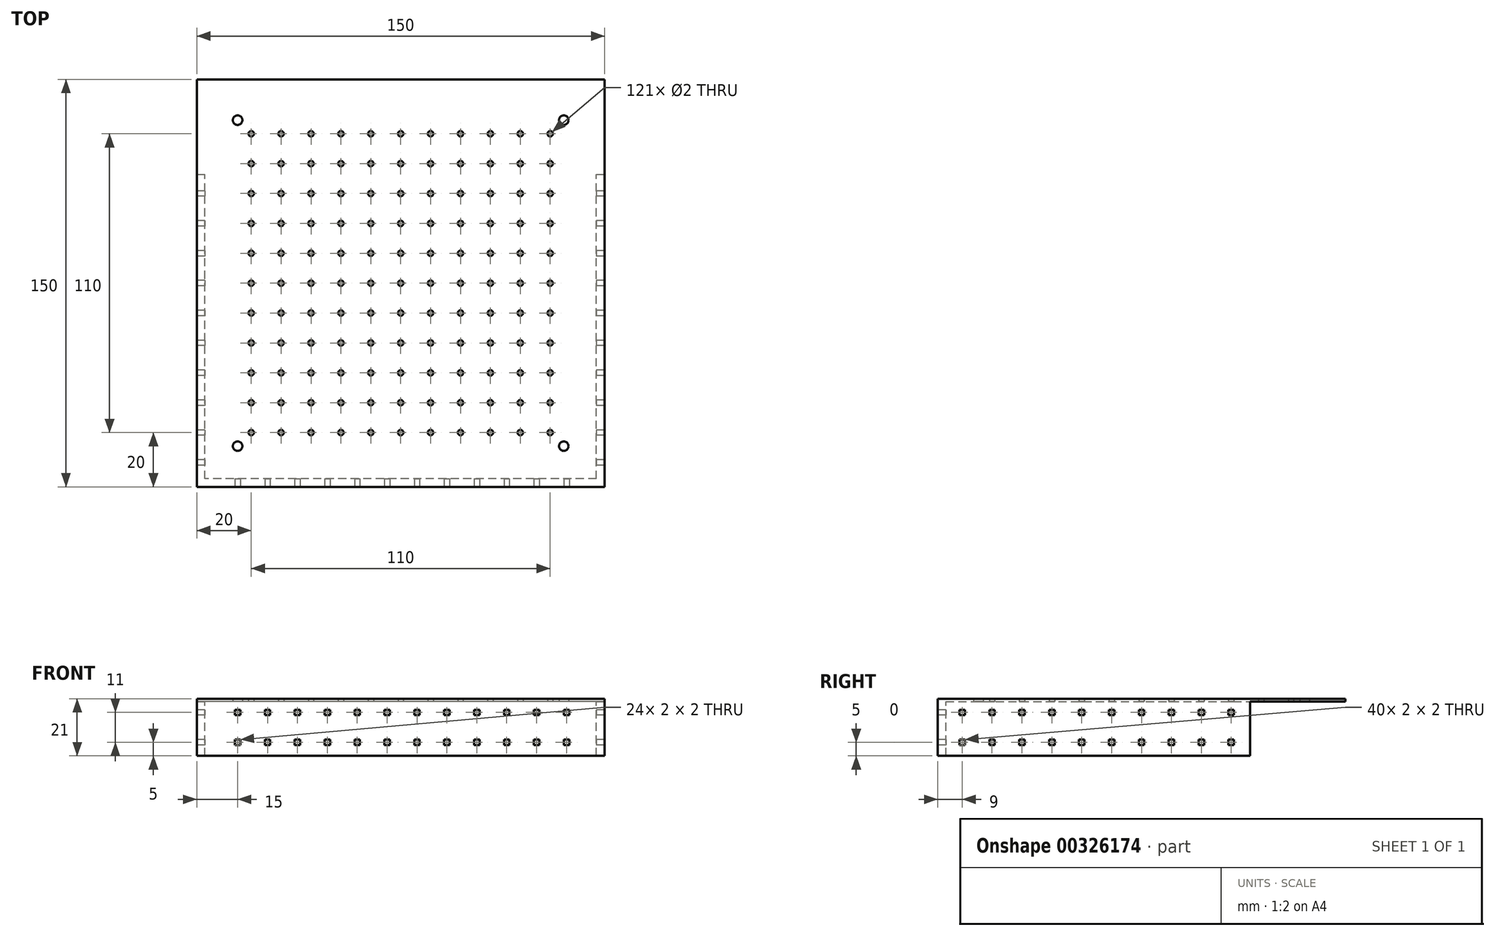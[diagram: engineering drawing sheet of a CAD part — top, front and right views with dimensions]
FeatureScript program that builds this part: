
annotation { "Feature Type Name" : "Feature", "Feature Type Description" : "" }
export const myFeature = defineFeature(function(context is Context, id is Id, definition is map)
    precondition{}
    {
        {
            var Q0;
            Q0=qCreatedBy(makeId("Top.planeOp"),FACE);
            var sketch = newSketch(context, id + "F0", { "sketchPlane" : qUnion([Q0])});
            skLineSegment(sketch, "E0.bottom", {"start": v(60, -60) * mm, "end": v(-60, -60) * mm, "construction": true});
            skLineSegment(sketch, "E0.top", {"start": v(60, 60) * mm, "end": v(-60, 60) * mm, "construction": true});
            skLineSegment(sketch, "E0.left", {"start": v(60, -60) * mm, "end": v(60, 60) * mm, "construction": true});
            skLineSegment(sketch, "E0.right", {"start": v(-60, -60) * mm, "end": v(-60, 60) * mm, "construction": true});
            skPoint(sketch, "E0.middle", {"position": v(0, 0) * mm});
            skCircle(sketch, "E1", {"center": v(60, -60) * mm, "radius": 1.75 * mm});
            skCircle(sketch, "E2.1.0", {"center": v(60, 60) * mm, "radius": 1.75 * mm});
            skCircle(sketch, "E2.2.0", {"center": v(-60, 60) * mm, "radius": 1.75 * mm});
            skCircle(sketch, "E2.3.0", {"center": v(-60, -60) * mm, "radius": 1.75 * mm});
            skLineSegment(sketch, "E3.bottom", {"start": v(75, -75) * mm, "end": v(-75, -75) * mm});
            skLineSegment(sketch, "E3.top", {"start": v(75, 75) * mm, "end": v(-75, 75) * mm});
            skLineSegment(sketch, "E3.left", {"start": v(75, -75) * mm, "end": v(75, 75) * mm});
            skLineSegment(sketch, "E3.right", {"start": v(-75, -75) * mm, "end": v(-75, 75) * mm});
            skLineSegment(sketch, "E4.bottom", {"start": v(72, -72) * mm, "end": v(-72, -72) * mm});
            skLineSegment(sketch, "E4.top", {"start": v(72, 72) * mm, "end": v(-72, 72) * mm});
            skLineSegment(sketch, "E4.left", {"start": v(72, -72) * mm, "end": v(72, 72) * mm});
            skLineSegment(sketch, "E4.right", {"start": v(-72, -72) * mm, "end": v(-72, 72) * mm});
            skLineSegment(sketch, "E5", {"start": v(-75, 0) * mm, "end": v(-72, 0) * mm});
            skLineSegment(sketch, "E6", {"start": v(72, 0) * mm, "end": v(75, 0) * mm});
            skLineSegment(sketch, "E7.bottom", {"start": v(55, -55) * mm, "end": v(-55, -55) * mm, "construction": true});
            skLineSegment(sketch, "E7.top", {"start": v(55, 55) * mm, "end": v(-55, 55) * mm, "construction": true});
            skLineSegment(sketch, "E7.left", {"start": v(55, -55) * mm, "end": v(55, 55) * mm, "construction": true});
            skLineSegment(sketch, "E7.right", {"start": v(-55, -55) * mm, "end": v(-55, 55) * mm, "construction": true});
            skCircle(sketch, "E8", {"center": v(-55, 55) * mm, "radius": 1 * mm});
            skCircle(sketch, "E9.0.1.0", {"center": v(-55, 44) * mm, "radius": 1 * mm});
            skCircle(sketch, "E9.0.2.0", {"center": v(-55, 33) * mm, "radius": 1 * mm});
            skCircle(sketch, "E9.0.3.0", {"center": v(-55, 22) * mm, "radius": 1 * mm});
            skCircle(sketch, "E9.0.4.0", {"center": v(-55, 11) * mm, "radius": 1 * mm});
            skCircle(sketch, "E9.0.5.0", {"center": v(-55, 0) * mm, "radius": 1 * mm});
            skCircle(sketch, "E9.0.6.0", {"center": v(-55, -11) * mm, "radius": 1 * mm});
            skCircle(sketch, "E9.0.7.0", {"center": v(-55, -22) * mm, "radius": 1 * mm});
            skCircle(sketch, "E9.0.8.0", {"center": v(-55, -33) * mm, "radius": 1 * mm});
            skCircle(sketch, "E9.0.9.0", {"center": v(-55, -44) * mm, "radius": 1 * mm});
            skCircle(sketch, "E9.0.10.0", {"center": v(-55, -55) * mm, "radius": 1 * mm});
            skCircle(sketch, "E9.1.0.0", {"center": v(-44, 55) * mm, "radius": 1 * mm});
            skCircle(sketch, "E9.1.1.0", {"center": v(-44, 44) * mm, "radius": 1 * mm});
            skCircle(sketch, "E9.1.2.0", {"center": v(-44, 33) * mm, "radius": 1 * mm});
            skCircle(sketch, "E9.1.3.0", {"center": v(-44, 22) * mm, "radius": 1 * mm});
            skCircle(sketch, "E9.1.4.0", {"center": v(-44, 11) * mm, "radius": 1 * mm});
            skCircle(sketch, "E9.1.5.0", {"center": v(-44, 0) * mm, "radius": 1 * mm});
            skCircle(sketch, "E9.1.6.0", {"center": v(-44, -11) * mm, "radius": 1 * mm});
            skCircle(sketch, "E9.1.7.0", {"center": v(-44, -22) * mm, "radius": 1 * mm});
            skCircle(sketch, "E9.1.8.0", {"center": v(-44, -33) * mm, "radius": 1 * mm});
            skCircle(sketch, "E9.1.9.0", {"center": v(-44, -44) * mm, "radius": 1 * mm});
            skCircle(sketch, "E9.1.10.0", {"center": v(-44, -55) * mm, "radius": 1 * mm});
            skCircle(sketch, "E9.2.0.0", {"center": v(-33, 55) * mm, "radius": 1 * mm});
            skCircle(sketch, "E9.2.1.0", {"center": v(-33, 44) * mm, "radius": 1 * mm});
            skCircle(sketch, "E9.2.2.0", {"center": v(-33, 33) * mm, "radius": 1 * mm});
            skCircle(sketch, "E9.2.3.0", {"center": v(-33, 22) * mm, "radius": 1 * mm});
            skCircle(sketch, "E9.2.4.0", {"center": v(-33, 11) * mm, "radius": 1 * mm});
            skCircle(sketch, "E9.2.5.0", {"center": v(-33, 0) * mm, "radius": 1 * mm});
            skCircle(sketch, "E9.2.6.0", {"center": v(-33, -11) * mm, "radius": 1 * mm});
            skCircle(sketch, "E9.2.7.0", {"center": v(-33, -22) * mm, "radius": 1 * mm});
            skCircle(sketch, "E9.2.8.0", {"center": v(-33, -33) * mm, "radius": 1 * mm});
            skCircle(sketch, "E9.2.9.0", {"center": v(-33, -44) * mm, "radius": 1 * mm});
            skCircle(sketch, "E9.2.10.0", {"center": v(-33, -55) * mm, "radius": 1 * mm});
            skCircle(sketch, "E9.3.0.0", {"center": v(-22, 55) * mm, "radius": 1 * mm});
            skCircle(sketch, "E9.3.1.0", {"center": v(-22, 44) * mm, "radius": 1 * mm});
            skCircle(sketch, "E9.3.2.0", {"center": v(-22, 33) * mm, "radius": 1 * mm});
            skCircle(sketch, "E9.3.3.0", {"center": v(-22, 22) * mm, "radius": 1 * mm});
            skCircle(sketch, "E9.3.4.0", {"center": v(-22, 11) * mm, "radius": 1 * mm});
            skCircle(sketch, "E9.3.5.0", {"center": v(-22, 0) * mm, "radius": 1 * mm});
            skCircle(sketch, "E9.3.6.0", {"center": v(-22, -11) * mm, "radius": 1 * mm});
            skCircle(sketch, "E9.3.7.0", {"center": v(-22, -22) * mm, "radius": 1 * mm});
            skCircle(sketch, "E9.3.8.0", {"center": v(-22, -33) * mm, "radius": 1 * mm});
            skCircle(sketch, "E9.3.9.0", {"center": v(-22, -44) * mm, "radius": 1 * mm});
            skCircle(sketch, "E9.3.10.0", {"center": v(-22, -55) * mm, "radius": 1 * mm});
            skCircle(sketch, "E9.4.0.0", {"center": v(-11, 55) * mm, "radius": 1 * mm});
            skCircle(sketch, "E9.4.1.0", {"center": v(-11, 44) * mm, "radius": 1 * mm});
            skCircle(sketch, "E9.4.2.0", {"center": v(-11, 33) * mm, "radius": 1 * mm});
            skCircle(sketch, "E9.4.3.0", {"center": v(-11, 22) * mm, "radius": 1 * mm});
            skCircle(sketch, "E9.4.4.0", {"center": v(-11, 11) * mm, "radius": 1 * mm});
            skCircle(sketch, "E9.4.5.0", {"center": v(-11, 0) * mm, "radius": 1 * mm});
            skCircle(sketch, "E9.4.6.0", {"center": v(-11, -11) * mm, "radius": 1 * mm});
            skCircle(sketch, "E9.4.7.0", {"center": v(-11, -22) * mm, "radius": 1 * mm});
            skCircle(sketch, "E9.4.8.0", {"center": v(-11, -33) * mm, "radius": 1 * mm});
            skCircle(sketch, "E9.4.9.0", {"center": v(-11, -44) * mm, "radius": 1 * mm});
            skCircle(sketch, "E9.4.10.0", {"center": v(-11, -55) * mm, "radius": 1 * mm});
            skCircle(sketch, "E9.5.0.0", {"center": v(0, 55) * mm, "radius": 1 * mm});
            skCircle(sketch, "E9.5.1.0", {"center": v(0, 44) * mm, "radius": 1 * mm});
            skCircle(sketch, "E9.5.2.0", {"center": v(0, 33) * mm, "radius": 1 * mm});
            skCircle(sketch, "E9.5.3.0", {"center": v(0, 22) * mm, "radius": 1 * mm});
            skCircle(sketch, "E9.5.4.0", {"center": v(0, 11) * mm, "radius": 1 * mm});
            skCircle(sketch, "E9.5.5.0", {"center": v(0, 0) * mm, "radius": 1 * mm});
            skCircle(sketch, "E9.5.6.0", {"center": v(0, -11) * mm, "radius": 1 * mm});
            skCircle(sketch, "E9.5.7.0", {"center": v(0, -22) * mm, "radius": 1 * mm});
            skCircle(sketch, "E9.5.8.0", {"center": v(0, -33) * mm, "radius": 1 * mm});
            skCircle(sketch, "E9.5.9.0", {"center": v(0, -44) * mm, "radius": 1 * mm});
            skCircle(sketch, "E9.5.10.0", {"center": v(0, -55) * mm, "radius": 1 * mm});
            skCircle(sketch, "E9.6.0.0", {"center": v(11, 55) * mm, "radius": 1 * mm});
            skCircle(sketch, "E9.6.1.0", {"center": v(11, 44) * mm, "radius": 1 * mm});
            skCircle(sketch, "E9.6.2.0", {"center": v(11, 33) * mm, "radius": 1 * mm});
            skCircle(sketch, "E9.6.3.0", {"center": v(11, 22) * mm, "radius": 1 * mm});
            skCircle(sketch, "E9.6.4.0", {"center": v(11, 11) * mm, "radius": 1 * mm});
            skCircle(sketch, "E9.6.5.0", {"center": v(11, 0) * mm, "radius": 1 * mm});
            skCircle(sketch, "E9.6.6.0", {"center": v(11, -11) * mm, "radius": 1 * mm});
            skCircle(sketch, "E9.6.7.0", {"center": v(11, -22) * mm, "radius": 1 * mm});
            skCircle(sketch, "E9.6.8.0", {"center": v(11, -33) * mm, "radius": 1 * mm});
            skCircle(sketch, "E9.6.9.0", {"center": v(11, -44) * mm, "radius": 1 * mm});
            skCircle(sketch, "E9.6.10.0", {"center": v(11, -55) * mm, "radius": 1 * mm});
            skCircle(sketch, "E9.7.0.0", {"center": v(22, 55) * mm, "radius": 1 * mm});
            skCircle(sketch, "E9.7.1.0", {"center": v(22, 44) * mm, "radius": 1 * mm});
            skCircle(sketch, "E9.7.2.0", {"center": v(22, 33) * mm, "radius": 1 * mm});
            skCircle(sketch, "E9.7.3.0", {"center": v(22, 22) * mm, "radius": 1 * mm});
            skCircle(sketch, "E9.7.4.0", {"center": v(22, 11) * mm, "radius": 1 * mm});
            skCircle(sketch, "E9.7.5.0", {"center": v(22, 0) * mm, "radius": 1 * mm});
            skCircle(sketch, "E9.7.6.0", {"center": v(22, -11) * mm, "radius": 1 * mm});
            skCircle(sketch, "E9.7.7.0", {"center": v(22, -22) * mm, "radius": 1 * mm});
            skCircle(sketch, "E9.7.8.0", {"center": v(22, -33) * mm, "radius": 1 * mm});
            skCircle(sketch, "E9.7.9.0", {"center": v(22, -44) * mm, "radius": 1 * mm});
            skCircle(sketch, "E9.7.10.0", {"center": v(22, -55) * mm, "radius": 1 * mm});
            skCircle(sketch, "E9.8.0.0", {"center": v(33, 55) * mm, "radius": 1 * mm});
            skCircle(sketch, "E9.8.1.0", {"center": v(33, 44) * mm, "radius": 1 * mm});
            skCircle(sketch, "E9.8.2.0", {"center": v(33, 33) * mm, "radius": 1 * mm});
            skCircle(sketch, "E9.8.3.0", {"center": v(33, 22) * mm, "radius": 1 * mm});
            skCircle(sketch, "E9.8.4.0", {"center": v(33, 11) * mm, "radius": 1 * mm});
            skCircle(sketch, "E9.8.5.0", {"center": v(33, 0) * mm, "radius": 1 * mm});
            skCircle(sketch, "E9.8.6.0", {"center": v(33, -11) * mm, "radius": 1 * mm});
            skCircle(sketch, "E9.8.7.0", {"center": v(33, -22) * mm, "radius": 1 * mm});
            skCircle(sketch, "E9.8.8.0", {"center": v(33, -33) * mm, "radius": 1 * mm});
            skCircle(sketch, "E9.8.9.0", {"center": v(33, -44) * mm, "radius": 1 * mm});
            skCircle(sketch, "E9.8.10.0", {"center": v(33, -55) * mm, "radius": 1 * mm});
            skCircle(sketch, "E9.9.0.0", {"center": v(44, 55) * mm, "radius": 1 * mm});
            skCircle(sketch, "E9.9.1.0", {"center": v(44, 44) * mm, "radius": 1 * mm});
            skCircle(sketch, "E9.9.2.0", {"center": v(44, 33) * mm, "radius": 1 * mm});
            skCircle(sketch, "E9.9.3.0", {"center": v(44, 22) * mm, "radius": 1 * mm});
            skCircle(sketch, "E9.9.4.0", {"center": v(44, 11) * mm, "radius": 1 * mm});
            skCircle(sketch, "E9.9.5.0", {"center": v(44, 0) * mm, "radius": 1 * mm});
            skCircle(sketch, "E9.9.6.0", {"center": v(44, -11) * mm, "radius": 1 * mm});
            skCircle(sketch, "E9.9.7.0", {"center": v(44, -22) * mm, "radius": 1 * mm});
            skCircle(sketch, "E9.9.8.0", {"center": v(44, -33) * mm, "radius": 1 * mm});
            skCircle(sketch, "E9.9.9.0", {"center": v(44, -44) * mm, "radius": 1 * mm});
            skCircle(sketch, "E9.9.10.0", {"center": v(44, -55) * mm, "radius": 1 * mm});
            skCircle(sketch, "E9.10.0.0", {"center": v(55, 55) * mm, "radius": 1 * mm});
            skCircle(sketch, "E9.10.1.0", {"center": v(55, 44) * mm, "radius": 1 * mm});
            skCircle(sketch, "E9.10.2.0", {"center": v(55, 33) * mm, "radius": 1 * mm});
            skCircle(sketch, "E9.10.3.0", {"center": v(55, 22) * mm, "radius": 1 * mm});
            skCircle(sketch, "E9.10.4.0", {"center": v(55, 11) * mm, "radius": 1 * mm});
            skCircle(sketch, "E9.10.5.0", {"center": v(55, 0) * mm, "radius": 1 * mm});
            skCircle(sketch, "E9.10.6.0", {"center": v(55, -11) * mm, "radius": 1 * mm});
            skCircle(sketch, "E9.10.7.0", {"center": v(55, -22) * mm, "radius": 1 * mm});
            skCircle(sketch, "E9.10.8.0", {"center": v(55, -33) * mm, "radius": 1 * mm});
            skCircle(sketch, "E9.10.9.0", {"center": v(55, -44) * mm, "radius": 1 * mm});
            skCircle(sketch, "E9.10.10.0", {"center": v(55, -55) * mm, "radius": 1 * mm});
            skLineSegment(sketch, "E9.direction1", {"start": v(-55, 55) * mm, "end": v(-44, 55) * mm, "construction": true});
            skLineSegment(sketch, "E9.direction2", {"start": v(-55, 55) * mm, "end": v(-55, 44) * mm, "construction": true});
            skLineSegment(sketch, "E10", {"start": v(-75, 40) * mm, "end": v(-72, 40) * mm});
            skLineSegment(sketch, "E11", {"start": v(72, 40) * mm, "end": v(75, 40) * mm});
            skSolve(sketch);
        }
        {
            var Q0;
            Q0=makeQuery(id+"F0.imprint","IMPRINT",FACE,{"disambiguationData":[TD([[makeQuery(id+"F0.imprint","IMPRINT",EDGE,{"derivedFrom":sQuery(id+"F0.wireOp",EDGE,"E1")}),-1.0]])]});
            var Q1;
            {var subQ2=sQuery(id+"F0.wireOp",EDGE,"E3.top");Q1=makeQuery(id+"F0.imprint","IMPRINT",FACE,{"disambiguationData":[TD([[makeQuery(id+"F0.imprint","IMPRINT",EDGE,{"derivedFrom":subQ2}),1.0]])]});}
            var Q2;
            {var subQ2=sQuery(id+"F0.wireOp",EDGE,"E3.bottom");Q2=makeQuery(id+"F0.imprint","IMPRINT",FACE,{"disambiguationData":[TD([[makeQuery(id+"F0.imprint","IMPRINT",EDGE,{"derivedFrom":subQ2}),-1.0]])]});}
            var Q3;
            {var subQ0=sQuery(id+"F0.wireOp",EDGE,"E5");Q3=makeQuery(id+"F0.imprint","IMPRINT",FACE,{"disambiguationData":[TD([[makeQuery(id+"F0.imprint","IMPRINT",EDGE,{"derivedFrom":subQ0}),1.0]])]});}
            var Q4;
            {var subQ0=sQuery(id+"F0.wireOp",EDGE,"E6");Q4=makeQuery(id+"F0.imprint","IMPRINT",FACE,{"disambiguationData":[TD([[makeQuery(id+"F0.imprint","IMPRINT",EDGE,{"derivedFrom":subQ0}),1.0]])]});}
            extrude(context, id + "F1", {"entities" : qUnion([Q0, Q1, Q2, Q3, Q4]), "depth" : 1 * mm});
        }
        {
            var Q0;
            {var subQ2=sQuery(id+"F0.wireOp",EDGE,"E3.bottom");Q0=makeQuery(id+"F0.imprint","IMPRINT",FACE,{"disambiguationData":[TD([[makeQuery(id+"F0.imprint","IMPRINT",EDGE,{"derivedFrom":subQ2}),-1.0]])]});}
            var Q1;
            {var subQ0=sQuery(id+"F0.wireOp",EDGE,"E6");Q1=makeQuery(id+"F0.imprint","IMPRINT",FACE,{"disambiguationData":[TD([[makeQuery(id+"F0.imprint","IMPRINT",EDGE,{"derivedFrom":subQ0}),1.0]])]});}
            var Q2;
            {var subQ0=sQuery(id+"F0.wireOp",EDGE,"E5");Q2=makeQuery(id+"F0.imprint","IMPRINT",FACE,{"disambiguationData":[TD([[makeQuery(id+"F0.imprint","IMPRINT",EDGE,{"derivedFrom":subQ0}),1.0]])]});}
            extrude(context, id + "F2", {"entities" : qUnion([Q0, Q1, Q2]), "operationType" : NewBodyOperationType.ADD, "oppositeDirection" : true, "depth" : 20 * mm});
        }
        {
            var Q0;
            {var subQ0=sQuery(id+"F0.wireOp",EDGE,"E3.right");Q0=makeQuery(id+"F2.boolean.opBoolean","MERGE",FACE,{"derivedFrom":[makeQuery(id+"F1.opExtrude","SWEPT_FACE",FACE,{"disambiguationData":[OSD([subQ0])]}),makeQuery(id+"F2.opExtrude","SWEPT_FACE",FACE,{"disambiguationData":[OSD([subQ0])]})]});}
            var sketch = newSketch(context, id + "F3", { "sketchPlane" : qUnion([Q0])});
            skLineSegment(sketch, "E12.bottom", {"start": v(-32, -5) * mm, "end": v(-34, -5) * mm});
            skLineSegment(sketch, "E12.top", {"start": v(-32, -3) * mm, "end": v(-34, -3) * mm});
            skLineSegment(sketch, "E12.left", {"start": v(-32, -5) * mm, "end": v(-32, -3) * mm});
            skLineSegment(sketch, "E12.right", {"start": v(-34, -5) * mm, "end": v(-34, -3) * mm});
            skPoint(sketch, "E12.middle", {"position": v(-33, -4) * mm});
            skLineSegment(sketch, "E13.0.1.0", {"start": v(-32, -16) * mm, "end": v(-32, -14) * mm});
            skLineSegment(sketch, "E13.0.1.1", {"start": v(-32, -14) * mm, "end": v(-34, -14) * mm});
            skLineSegment(sketch, "E13.0.1.2", {"start": v(-34, -16) * mm, "end": v(-34, -14) * mm});
            skLineSegment(sketch, "E13.0.1.3", {"start": v(-32, -16) * mm, "end": v(-34, -16) * mm});
            skLineSegment(sketch, "E13.1.0.0", {"start": v(-21, -5) * mm, "end": v(-21, -3) * mm});
            skLineSegment(sketch, "E13.1.0.1", {"start": v(-21, -3) * mm, "end": v(-23, -3) * mm});
            skLineSegment(sketch, "E13.1.0.2", {"start": v(-23, -5) * mm, "end": v(-23, -3) * mm});
            skLineSegment(sketch, "E13.1.0.3", {"start": v(-21, -5) * mm, "end": v(-23, -5) * mm});
            skLineSegment(sketch, "E13.1.1.0", {"start": v(-21, -16) * mm, "end": v(-21, -14) * mm});
            skLineSegment(sketch, "E13.1.1.1", {"start": v(-21, -14) * mm, "end": v(-23, -14) * mm});
            skLineSegment(sketch, "E13.1.1.2", {"start": v(-23, -16) * mm, "end": v(-23, -14) * mm});
            skLineSegment(sketch, "E13.1.1.3", {"start": v(-21, -16) * mm, "end": v(-23, -16) * mm});
            skLineSegment(sketch, "E13.2.0.0", {"start": v(-10, -5) * mm, "end": v(-10, -3) * mm});
            skLineSegment(sketch, "E13.2.0.1", {"start": v(-10, -3) * mm, "end": v(-12, -3) * mm});
            skLineSegment(sketch, "E13.2.0.2", {"start": v(-12, -5) * mm, "end": v(-12, -3) * mm});
            skLineSegment(sketch, "E13.2.0.3", {"start": v(-10, -5) * mm, "end": v(-12, -5) * mm});
            skLineSegment(sketch, "E13.2.1.0", {"start": v(-10, -16) * mm, "end": v(-10, -14) * mm});
            skLineSegment(sketch, "E13.2.1.1", {"start": v(-10, -14) * mm, "end": v(-12, -14) * mm});
            skLineSegment(sketch, "E13.2.1.2", {"start": v(-12, -16) * mm, "end": v(-12, -14) * mm});
            skLineSegment(sketch, "E13.2.1.3", {"start": v(-10, -16) * mm, "end": v(-12, -16) * mm});
            skLineSegment(sketch, "E13.3.0.0", {"start": v(1, -5) * mm, "end": v(1, -3) * mm});
            skLineSegment(sketch, "E13.3.0.1", {"start": v(1, -3) * mm, "end": v(-1, -3) * mm});
            skLineSegment(sketch, "E13.3.0.2", {"start": v(-1, -5) * mm, "end": v(-1, -3) * mm});
            skLineSegment(sketch, "E13.3.0.3", {"start": v(1, -5) * mm, "end": v(-1, -5) * mm});
            skLineSegment(sketch, "E13.3.1.0", {"start": v(1, -16) * mm, "end": v(1, -14) * mm});
            skLineSegment(sketch, "E13.3.1.1", {"start": v(1, -14) * mm, "end": v(-1, -14) * mm});
            skLineSegment(sketch, "E13.3.1.2", {"start": v(-1, -16) * mm, "end": v(-1, -14) * mm});
            skLineSegment(sketch, "E13.3.1.3", {"start": v(1, -16) * mm, "end": v(-1, -16) * mm});
            skLineSegment(sketch, "E13.4.0.0", {"start": v(12, -5) * mm, "end": v(12, -3) * mm});
            skLineSegment(sketch, "E13.4.0.1", {"start": v(12, -3) * mm, "end": v(10, -3) * mm});
            skLineSegment(sketch, "E13.4.0.2", {"start": v(10, -5) * mm, "end": v(10, -3) * mm});
            skLineSegment(sketch, "E13.4.0.3", {"start": v(12, -5) * mm, "end": v(10, -5) * mm});
            skLineSegment(sketch, "E13.4.1.0", {"start": v(12, -16) * mm, "end": v(12, -14) * mm});
            skLineSegment(sketch, "E13.4.1.1", {"start": v(12, -14) * mm, "end": v(10, -14) * mm});
            skLineSegment(sketch, "E13.4.1.2", {"start": v(10, -16) * mm, "end": v(10, -14) * mm});
            skLineSegment(sketch, "E13.4.1.3", {"start": v(12, -16) * mm, "end": v(10, -16) * mm});
            skLineSegment(sketch, "E13.5.0.0", {"start": v(23, -5) * mm, "end": v(23, -3) * mm});
            skLineSegment(sketch, "E13.5.0.1", {"start": v(23, -3) * mm, "end": v(21, -3) * mm});
            skLineSegment(sketch, "E13.5.0.2", {"start": v(21, -5) * mm, "end": v(21, -3) * mm});
            skLineSegment(sketch, "E13.5.0.3", {"start": v(23, -5) * mm, "end": v(21, -5) * mm});
            skLineSegment(sketch, "E13.5.1.0", {"start": v(23, -16) * mm, "end": v(23, -14) * mm});
            skLineSegment(sketch, "E13.5.1.1", {"start": v(23, -14) * mm, "end": v(21, -14) * mm});
            skLineSegment(sketch, "E13.5.1.2", {"start": v(21, -16) * mm, "end": v(21, -14) * mm});
            skLineSegment(sketch, "E13.5.1.3", {"start": v(23, -16) * mm, "end": v(21, -16) * mm});
            skLineSegment(sketch, "E13.6.0.0", {"start": v(34, -5) * mm, "end": v(34, -3) * mm});
            skLineSegment(sketch, "E13.6.0.1", {"start": v(34, -3) * mm, "end": v(32, -3) * mm});
            skLineSegment(sketch, "E13.6.0.2", {"start": v(32, -5) * mm, "end": v(32, -3) * mm});
            skLineSegment(sketch, "E13.6.0.3", {"start": v(34, -5) * mm, "end": v(32, -5) * mm});
            skLineSegment(sketch, "E13.6.1.0", {"start": v(34, -16) * mm, "end": v(34, -14) * mm});
            skLineSegment(sketch, "E13.6.1.1", {"start": v(34, -14) * mm, "end": v(32, -14) * mm});
            skLineSegment(sketch, "E13.6.1.2", {"start": v(32, -16) * mm, "end": v(32, -14) * mm});
            skLineSegment(sketch, "E13.6.1.3", {"start": v(34, -16) * mm, "end": v(32, -16) * mm});
            skLineSegment(sketch, "E13.7.0.0", {"start": v(45, -5) * mm, "end": v(45, -3) * mm});
            skLineSegment(sketch, "E13.7.0.1", {"start": v(45, -3) * mm, "end": v(43, -3) * mm});
            skLineSegment(sketch, "E13.7.0.2", {"start": v(43, -5) * mm, "end": v(43, -3) * mm});
            skLineSegment(sketch, "E13.7.0.3", {"start": v(45, -5) * mm, "end": v(43, -5) * mm});
            skLineSegment(sketch, "E13.7.1.0", {"start": v(45, -16) * mm, "end": v(45, -14) * mm});
            skLineSegment(sketch, "E13.7.1.1", {"start": v(45, -14) * mm, "end": v(43, -14) * mm});
            skLineSegment(sketch, "E13.7.1.2", {"start": v(43, -16) * mm, "end": v(43, -14) * mm});
            skLineSegment(sketch, "E13.7.1.3", {"start": v(45, -16) * mm, "end": v(43, -16) * mm});
            skLineSegment(sketch, "E13.8.0.0", {"start": v(56, -5) * mm, "end": v(56, -3) * mm});
            skLineSegment(sketch, "E13.8.0.1", {"start": v(56, -3) * mm, "end": v(54, -3) * mm});
            skLineSegment(sketch, "E13.8.0.2", {"start": v(54, -5) * mm, "end": v(54, -3) * mm});
            skLineSegment(sketch, "E13.8.0.3", {"start": v(56, -5) * mm, "end": v(54, -5) * mm});
            skLineSegment(sketch, "E13.8.1.0", {"start": v(56, -16) * mm, "end": v(56, -14) * mm});
            skLineSegment(sketch, "E13.8.1.1", {"start": v(56, -14) * mm, "end": v(54, -14) * mm});
            skLineSegment(sketch, "E13.8.1.2", {"start": v(54, -16) * mm, "end": v(54, -14) * mm});
            skLineSegment(sketch, "E13.8.1.3", {"start": v(56, -16) * mm, "end": v(54, -16) * mm});
            skLineSegment(sketch, "E13.9.0.0", {"start": v(67, -5) * mm, "end": v(67, -3) * mm});
            skLineSegment(sketch, "E13.9.0.1", {"start": v(67, -3) * mm, "end": v(65, -3) * mm});
            skLineSegment(sketch, "E13.9.0.2", {"start": v(65, -5) * mm, "end": v(65, -3) * mm});
            skLineSegment(sketch, "E13.9.0.3", {"start": v(67, -5) * mm, "end": v(65, -5) * mm});
            skLineSegment(sketch, "E13.9.1.0", {"start": v(67, -16) * mm, "end": v(67, -14) * mm});
            skLineSegment(sketch, "E13.9.1.1", {"start": v(67, -14) * mm, "end": v(65, -14) * mm});
            skLineSegment(sketch, "E13.9.1.2", {"start": v(65, -16) * mm, "end": v(65, -14) * mm});
            skLineSegment(sketch, "E13.9.1.3", {"start": v(67, -16) * mm, "end": v(65, -16) * mm});
            skLineSegment(sketch, "E13.direction1", {"start": v(-32, -5) * mm, "end": v(-21, -5) * mm, "construction": true});
            skLineSegment(sketch, "E13.direction2", {"start": v(-32, -5) * mm, "end": v(-32, -16) * mm, "construction": true});
            skSolve(sketch);
        }
        {
            var Q0;
            Q0=makeQuery(id+"F3.imprint","IMPRINT",FACE,{"disambiguationData":[TD([[makeQuery(id+"F3.imprint","IMPRINT",EDGE,{"derivedFrom":sQuery(id+"F3.wireOp",EDGE,"E12.bottom")}),-1.0]])]});
            var Q1;
            Q1=makeQuery(id+"F3.imprint","IMPRINT",FACE,{"disambiguationData":[TD([[makeQuery(id+"F3.imprint","IMPRINT",EDGE,{"derivedFrom":sQuery(id+"F3.wireOp",EDGE,"E13.0.1.0")}),1.0]])]});
            var Q2;
            Q2=makeQuery(id+"F3.imprint","IMPRINT",FACE,{"disambiguationData":[TD([[makeQuery(id+"F3.imprint","IMPRINT",EDGE,{"derivedFrom":sQuery(id+"F3.wireOp",EDGE,"E13.1.0.0")}),1.0]])]});
            var Q3;
            Q3=makeQuery(id+"F3.imprint","IMPRINT",FACE,{"disambiguationData":[TD([[makeQuery(id+"F3.imprint","IMPRINT",EDGE,{"derivedFrom":sQuery(id+"F3.wireOp",EDGE,"E13.2.0.0")}),1.0]])]});
            var Q4;
            Q4=makeQuery(id+"F3.imprint","IMPRINT",FACE,{"disambiguationData":[TD([[makeQuery(id+"F3.imprint","IMPRINT",EDGE,{"derivedFrom":sQuery(id+"F3.wireOp",EDGE,"E13.2.1.0")}),1.0]])]});
            var Q5;
            Q5=makeQuery(id+"F3.imprint","IMPRINT",FACE,{"disambiguationData":[TD([[makeQuery(id+"F3.imprint","IMPRINT",EDGE,{"derivedFrom":sQuery(id+"F3.wireOp",EDGE,"E13.1.1.0")}),1.0]])]});
            var Q6;
            Q6=makeQuery(id+"F3.imprint","IMPRINT",FACE,{"disambiguationData":[TD([[makeQuery(id+"F3.imprint","IMPRINT",EDGE,{"derivedFrom":sQuery(id+"F3.wireOp",EDGE,"E13.3.1.0")}),1.0]])]});
            var Q7;
            Q7=makeQuery(id+"F3.imprint","IMPRINT",FACE,{"disambiguationData":[TD([[makeQuery(id+"F3.imprint","IMPRINT",EDGE,{"derivedFrom":sQuery(id+"F3.wireOp",EDGE,"E13.4.1.0")}),1.0]])]});
            var Q8;
            Q8=makeQuery(id+"F3.imprint","IMPRINT",FACE,{"disambiguationData":[TD([[makeQuery(id+"F3.imprint","IMPRINT",EDGE,{"derivedFrom":sQuery(id+"F3.wireOp",EDGE,"E13.5.1.0")}),1.0]])]});
            var Q9;
            Q9=makeQuery(id+"F3.imprint","IMPRINT",FACE,{"disambiguationData":[TD([[makeQuery(id+"F3.imprint","IMPRINT",EDGE,{"derivedFrom":sQuery(id+"F3.wireOp",EDGE,"E13.6.1.0")}),1.0]])]});
            var Q10;
            Q10=makeQuery(id+"F3.imprint","IMPRINT",FACE,{"disambiguationData":[TD([[makeQuery(id+"F3.imprint","IMPRINT",EDGE,{"derivedFrom":sQuery(id+"F3.wireOp",EDGE,"E13.7.1.0")}),1.0]])]});
            var Q11;
            Q11=makeQuery(id+"F3.imprint","IMPRINT",FACE,{"disambiguationData":[TD([[makeQuery(id+"F3.imprint","IMPRINT",EDGE,{"derivedFrom":sQuery(id+"F3.wireOp",EDGE,"E13.8.1.0")}),1.0]])]});
            var Q12;
            Q12=makeQuery(id+"F3.imprint","IMPRINT",FACE,{"disambiguationData":[TD([[makeQuery(id+"F3.imprint","IMPRINT",EDGE,{"derivedFrom":sQuery(id+"F3.wireOp",EDGE,"E13.9.1.0")}),1.0]])]});
            var Q13;
            Q13=makeQuery(id+"F3.imprint","IMPRINT",FACE,{"disambiguationData":[TD([[makeQuery(id+"F3.imprint","IMPRINT",EDGE,{"derivedFrom":sQuery(id+"F3.wireOp",EDGE,"E13.9.0.0")}),1.0]])]});
            var Q14;
            Q14=makeQuery(id+"F3.imprint","IMPRINT",FACE,{"disambiguationData":[TD([[makeQuery(id+"F3.imprint","IMPRINT",EDGE,{"derivedFrom":sQuery(id+"F3.wireOp",EDGE,"E13.8.0.0")}),1.0]])]});
            var Q15;
            Q15=makeQuery(id+"F3.imprint","IMPRINT",FACE,{"disambiguationData":[TD([[makeQuery(id+"F3.imprint","IMPRINT",EDGE,{"derivedFrom":sQuery(id+"F3.wireOp",EDGE,"E13.7.0.0")}),1.0]])]});
            var Q16;
            Q16=makeQuery(id+"F3.imprint","IMPRINT",FACE,{"disambiguationData":[TD([[makeQuery(id+"F3.imprint","IMPRINT",EDGE,{"derivedFrom":sQuery(id+"F3.wireOp",EDGE,"E13.6.0.0")}),1.0]])]});
            var Q17;
            Q17=makeQuery(id+"F3.imprint","IMPRINT",FACE,{"disambiguationData":[TD([[makeQuery(id+"F3.imprint","IMPRINT",EDGE,{"derivedFrom":sQuery(id+"F3.wireOp",EDGE,"E13.5.0.0")}),1.0]])]});
            var Q18;
            Q18=makeQuery(id+"F3.imprint","IMPRINT",FACE,{"disambiguationData":[TD([[makeQuery(id+"F3.imprint","IMPRINT",EDGE,{"derivedFrom":sQuery(id+"F3.wireOp",EDGE,"E13.4.0.0")}),1.0]])]});
            var Q19;
            Q19=makeQuery(id+"F3.imprint","IMPRINT",FACE,{"disambiguationData":[TD([[makeQuery(id+"F3.imprint","IMPRINT",EDGE,{"derivedFrom":sQuery(id+"F3.wireOp",EDGE,"E13.3.0.0")}),1.0]])]});
            extrude(context, id + "F4", {"entities" : qUnion([Q0, Q1, Q2, Q3, Q4, Q5, Q6, Q7, Q8, Q9, Q10, Q11, Q12, Q13, Q14, Q15, Q16, Q17, Q18, Q19]), "operationType" : NewBodyOperationType.REMOVE, "oppositeDirection" : true, "depth" : 200 * mm});
        }
        {
            var Q0;
            {var subQ0=sQuery(id+"F0.wireOp",EDGE,"E3.bottom");Q0=makeQuery(id+"F2.boolean.opBoolean","MERGE",FACE,{"derivedFrom":[makeQuery(id+"F1.opExtrude","SWEPT_FACE",FACE,{"disambiguationData":[OSD([subQ0])]}),makeQuery(id+"F2.opExtrude","SWEPT_FACE",FACE,{"disambiguationData":[OSD([subQ0])]})]});}
            var sketch = newSketch(context, id + "F5", { "sketchPlane" : qUnion([Q0])});
            skLineSegment(sketch, "E14.bottom", {"start": v(-59, -5) * mm, "end": v(-61, -5) * mm});
            skLineSegment(sketch, "E14.top", {"start": v(-59, -3) * mm, "end": v(-61, -3) * mm});
            skLineSegment(sketch, "E14.left", {"start": v(-59, -5) * mm, "end": v(-59, -3) * mm});
            skLineSegment(sketch, "E14.right", {"start": v(-61, -5) * mm, "end": v(-61, -3) * mm});
            skPoint(sketch, "E14.middle", {"position": v(-60, -4) * mm});
            skLineSegment(sketch, "E15.0.1.0", {"start": v(-59, -16) * mm, "end": v(-59, -14) * mm});
            skLineSegment(sketch, "E15.0.1.1", {"start": v(-59, -14) * mm, "end": v(-61, -14) * mm});
            skLineSegment(sketch, "E15.0.1.2", {"start": v(-61, -16) * mm, "end": v(-61, -14) * mm});
            skLineSegment(sketch, "E15.0.1.3", {"start": v(-59, -16) * mm, "end": v(-61, -16) * mm});
            skLineSegment(sketch, "E15.1.0.0", {"start": v(-48, -5) * mm, "end": v(-48, -3) * mm});
            skLineSegment(sketch, "E15.1.0.1", {"start": v(-48, -3) * mm, "end": v(-50, -3) * mm});
            skLineSegment(sketch, "E15.1.0.2", {"start": v(-50, -5) * mm, "end": v(-50, -3) * mm});
            skLineSegment(sketch, "E15.1.0.3", {"start": v(-48, -5) * mm, "end": v(-50, -5) * mm});
            skLineSegment(sketch, "E15.1.1.0", {"start": v(-48, -16) * mm, "end": v(-48, -14) * mm});
            skLineSegment(sketch, "E15.1.1.1", {"start": v(-48, -14) * mm, "end": v(-50, -14) * mm});
            skLineSegment(sketch, "E15.1.1.2", {"start": v(-50, -16) * mm, "end": v(-50, -14) * mm});
            skLineSegment(sketch, "E15.1.1.3", {"start": v(-48, -16) * mm, "end": v(-50, -16) * mm});
            skLineSegment(sketch, "E15.2.0.0", {"start": v(-37, -5) * mm, "end": v(-37, -3) * mm});
            skLineSegment(sketch, "E15.2.0.1", {"start": v(-37, -3) * mm, "end": v(-39, -3) * mm});
            skLineSegment(sketch, "E15.2.0.2", {"start": v(-39, -5) * mm, "end": v(-39, -3) * mm});
            skLineSegment(sketch, "E15.2.0.3", {"start": v(-37, -5) * mm, "end": v(-39, -5) * mm});
            skLineSegment(sketch, "E15.2.1.0", {"start": v(-37, -16) * mm, "end": v(-37, -14) * mm});
            skLineSegment(sketch, "E15.2.1.1", {"start": v(-37, -14) * mm, "end": v(-39, -14) * mm});
            skLineSegment(sketch, "E15.2.1.2", {"start": v(-39, -16) * mm, "end": v(-39, -14) * mm});
            skLineSegment(sketch, "E15.2.1.3", {"start": v(-37, -16) * mm, "end": v(-39, -16) * mm});
            skLineSegment(sketch, "E15.3.0.0", {"start": v(-26, -5) * mm, "end": v(-26, -3) * mm});
            skLineSegment(sketch, "E15.3.0.1", {"start": v(-26, -3) * mm, "end": v(-28, -3) * mm});
            skLineSegment(sketch, "E15.3.0.2", {"start": v(-28, -5) * mm, "end": v(-28, -3) * mm});
            skLineSegment(sketch, "E15.3.0.3", {"start": v(-26, -5) * mm, "end": v(-28, -5) * mm});
            skLineSegment(sketch, "E15.3.1.0", {"start": v(-26, -16) * mm, "end": v(-26, -14) * mm});
            skLineSegment(sketch, "E15.3.1.1", {"start": v(-26, -14) * mm, "end": v(-28, -14) * mm});
            skLineSegment(sketch, "E15.3.1.2", {"start": v(-28, -16) * mm, "end": v(-28, -14) * mm});
            skLineSegment(sketch, "E15.3.1.3", {"start": v(-26, -16) * mm, "end": v(-28, -16) * mm});
            skLineSegment(sketch, "E15.4.0.0", {"start": v(-15, -5) * mm, "end": v(-15, -3) * mm});
            skLineSegment(sketch, "E15.4.0.1", {"start": v(-15, -3) * mm, "end": v(-17, -3) * mm});
            skLineSegment(sketch, "E15.4.0.2", {"start": v(-17, -5) * mm, "end": v(-17, -3) * mm});
            skLineSegment(sketch, "E15.4.0.3", {"start": v(-15, -5) * mm, "end": v(-17, -5) * mm});
            skLineSegment(sketch, "E15.4.1.0", {"start": v(-15, -16) * mm, "end": v(-15, -14) * mm});
            skLineSegment(sketch, "E15.4.1.1", {"start": v(-15, -14) * mm, "end": v(-17, -14) * mm});
            skLineSegment(sketch, "E15.4.1.2", {"start": v(-17, -16) * mm, "end": v(-17, -14) * mm});
            skLineSegment(sketch, "E15.4.1.3", {"start": v(-15, -16) * mm, "end": v(-17, -16) * mm});
            skLineSegment(sketch, "E15.5.0.0", {"start": v(-4, -5) * mm, "end": v(-4, -3) * mm});
            skLineSegment(sketch, "E15.5.0.1", {"start": v(-4, -3) * mm, "end": v(-6, -3) * mm});
            skLineSegment(sketch, "E15.5.0.2", {"start": v(-6, -5) * mm, "end": v(-6, -3) * mm});
            skLineSegment(sketch, "E15.5.0.3", {"start": v(-4, -5) * mm, "end": v(-6, -5) * mm});
            skLineSegment(sketch, "E15.5.1.0", {"start": v(-4, -16) * mm, "end": v(-4, -14) * mm});
            skLineSegment(sketch, "E15.5.1.1", {"start": v(-4, -14) * mm, "end": v(-6, -14) * mm});
            skLineSegment(sketch, "E15.5.1.2", {"start": v(-6, -16) * mm, "end": v(-6, -14) * mm});
            skLineSegment(sketch, "E15.5.1.3", {"start": v(-4, -16) * mm, "end": v(-6, -16) * mm});
            skLineSegment(sketch, "E15.6.0.0", {"start": v(7, -5) * mm, "end": v(7, -3) * mm});
            skLineSegment(sketch, "E15.6.0.1", {"start": v(7, -3) * mm, "end": v(5, -3) * mm});
            skLineSegment(sketch, "E15.6.0.2", {"start": v(5, -5) * mm, "end": v(5, -3) * mm});
            skLineSegment(sketch, "E15.6.0.3", {"start": v(7, -5) * mm, "end": v(5, -5) * mm});
            skLineSegment(sketch, "E15.6.1.0", {"start": v(7, -16) * mm, "end": v(7, -14) * mm});
            skLineSegment(sketch, "E15.6.1.1", {"start": v(7, -14) * mm, "end": v(5, -14) * mm});
            skLineSegment(sketch, "E15.6.1.2", {"start": v(5, -16) * mm, "end": v(5, -14) * mm});
            skLineSegment(sketch, "E15.6.1.3", {"start": v(7, -16) * mm, "end": v(5, -16) * mm});
            skLineSegment(sketch, "E15.7.0.0", {"start": v(18, -5) * mm, "end": v(18, -3) * mm});
            skLineSegment(sketch, "E15.7.0.1", {"start": v(18, -3) * mm, "end": v(16, -3) * mm});
            skLineSegment(sketch, "E15.7.0.2", {"start": v(16, -5) * mm, "end": v(16, -3) * mm});
            skLineSegment(sketch, "E15.7.0.3", {"start": v(18, -5) * mm, "end": v(16, -5) * mm});
            skLineSegment(sketch, "E15.7.1.0", {"start": v(18, -16) * mm, "end": v(18, -14) * mm});
            skLineSegment(sketch, "E15.7.1.1", {"start": v(18, -14) * mm, "end": v(16, -14) * mm});
            skLineSegment(sketch, "E15.7.1.2", {"start": v(16, -16) * mm, "end": v(16, -14) * mm});
            skLineSegment(sketch, "E15.7.1.3", {"start": v(18, -16) * mm, "end": v(16, -16) * mm});
            skLineSegment(sketch, "E15.8.0.0", {"start": v(29, -5) * mm, "end": v(29, -3) * mm});
            skLineSegment(sketch, "E15.8.0.1", {"start": v(29, -3) * mm, "end": v(27, -3) * mm});
            skLineSegment(sketch, "E15.8.0.2", {"start": v(27, -5) * mm, "end": v(27, -3) * mm});
            skLineSegment(sketch, "E15.8.0.3", {"start": v(29, -5) * mm, "end": v(27, -5) * mm});
            skLineSegment(sketch, "E15.8.1.0", {"start": v(29, -16) * mm, "end": v(29, -14) * mm});
            skLineSegment(sketch, "E15.8.1.1", {"start": v(29, -14) * mm, "end": v(27, -14) * mm});
            skLineSegment(sketch, "E15.8.1.2", {"start": v(27, -16) * mm, "end": v(27, -14) * mm});
            skLineSegment(sketch, "E15.8.1.3", {"start": v(29, -16) * mm, "end": v(27, -16) * mm});
            skLineSegment(sketch, "E15.9.0.0", {"start": v(40, -5) * mm, "end": v(40, -3) * mm});
            skLineSegment(sketch, "E15.9.0.1", {"start": v(40, -3) * mm, "end": v(38, -3) * mm});
            skLineSegment(sketch, "E15.9.0.2", {"start": v(38, -5) * mm, "end": v(38, -3) * mm});
            skLineSegment(sketch, "E15.9.0.3", {"start": v(40, -5) * mm, "end": v(38, -5) * mm});
            skLineSegment(sketch, "E15.9.1.0", {"start": v(40, -16) * mm, "end": v(40, -14) * mm});
            skLineSegment(sketch, "E15.9.1.1", {"start": v(40, -14) * mm, "end": v(38, -14) * mm});
            skLineSegment(sketch, "E15.9.1.2", {"start": v(38, -16) * mm, "end": v(38, -14) * mm});
            skLineSegment(sketch, "E15.9.1.3", {"start": v(40, -16) * mm, "end": v(38, -16) * mm});
            skLineSegment(sketch, "E15.direction1", {"start": v(-59, -5) * mm, "end": v(-48, -5) * mm, "construction": true});
            skLineSegment(sketch, "E15.direction2", {"start": v(-59, -5) * mm, "end": v(-59, -16) * mm, "construction": true});
            skLineSegment(sketch, "E16.0.10.0", {"start": v(51, -5) * mm, "end": v(51, -3) * mm});
            skLineSegment(sketch, "E16.3.10.0", {"start": v(51, -3) * mm, "end": v(49, -3) * mm});
            skLineSegment(sketch, "E16.6.10.0", {"start": v(49, -5) * mm, "end": v(49, -3) * mm});
            skLineSegment(sketch, "E16.9.10.0", {"start": v(51, -5) * mm, "end": v(49, -5) * mm});
            skLineSegment(sketch, "E16.0.10.1", {"start": v(51, -16) * mm, "end": v(51, -14) * mm});
            skLineSegment(sketch, "E16.3.10.1", {"start": v(51, -14) * mm, "end": v(49, -14) * mm});
            skLineSegment(sketch, "E16.6.10.1", {"start": v(49, -16) * mm, "end": v(49, -14) * mm});
            skLineSegment(sketch, "E16.9.10.1", {"start": v(51, -16) * mm, "end": v(49, -16) * mm});
            skLineSegment(sketch, "E17.0.11.0", {"start": v(62, -5) * mm, "end": v(62, -3) * mm});
            skLineSegment(sketch, "E17.3.11.0", {"start": v(62, -3) * mm, "end": v(60, -3) * mm});
            skLineSegment(sketch, "E17.6.11.0", {"start": v(60, -5) * mm, "end": v(60, -3) * mm});
            skLineSegment(sketch, "E17.9.11.0", {"start": v(62, -5) * mm, "end": v(60, -5) * mm});
            skLineSegment(sketch, "E17.0.11.1", {"start": v(62, -16) * mm, "end": v(62, -14) * mm});
            skLineSegment(sketch, "E17.3.11.1", {"start": v(62, -14) * mm, "end": v(60, -14) * mm});
            skLineSegment(sketch, "E17.6.11.1", {"start": v(60, -16) * mm, "end": v(60, -14) * mm});
            skLineSegment(sketch, "E17.9.11.1", {"start": v(62, -16) * mm, "end": v(60, -16) * mm});
            skSolve(sketch);
        }
        {
            var Q0;
            Q0=makeQuery(id+"F5.imprint","IMPRINT",FACE,{"disambiguationData":[TD([[makeQuery(id+"F5.imprint","IMPRINT",EDGE,{"derivedFrom":sQuery(id+"F5.wireOp",EDGE,"E14.bottom")}),-1.0]])]});
            var Q1;
            Q1=makeQuery(id+"F5.imprint","IMPRINT",FACE,{"disambiguationData":[TD([[makeQuery(id+"F5.imprint","IMPRINT",EDGE,{"derivedFrom":sQuery(id+"F5.wireOp",EDGE,"E15.0.1.0")}),1.0]])]});
            var Q2;
            Q2=makeQuery(id+"F5.imprint","IMPRINT",FACE,{"disambiguationData":[TD([[makeQuery(id+"F5.imprint","IMPRINT",EDGE,{"derivedFrom":sQuery(id+"F5.wireOp",EDGE,"E15.1.0.0")}),1.0]])]});
            var Q3;
            Q3=makeQuery(id+"F5.imprint","IMPRINT",FACE,{"disambiguationData":[TD([[makeQuery(id+"F5.imprint","IMPRINT",EDGE,{"derivedFrom":sQuery(id+"F5.wireOp",EDGE,"E15.1.1.0")}),1.0]])]});
            var Q4;
            Q4=makeQuery(id+"F5.imprint","IMPRINT",FACE,{"disambiguationData":[TD([[makeQuery(id+"F5.imprint","IMPRINT",EDGE,{"derivedFrom":sQuery(id+"F5.wireOp",EDGE,"E15.2.0.0")}),1.0]])]});
            var Q5;
            Q5=makeQuery(id+"F5.imprint","IMPRINT",FACE,{"disambiguationData":[TD([[makeQuery(id+"F5.imprint","IMPRINT",EDGE,{"derivedFrom":sQuery(id+"F5.wireOp",EDGE,"E15.2.1.0")}),1.0]])]});
            var Q6;
            Q6=makeQuery(id+"F5.imprint","IMPRINT",FACE,{"disambiguationData":[TD([[makeQuery(id+"F5.imprint","IMPRINT",EDGE,{"derivedFrom":sQuery(id+"F5.wireOp",EDGE,"E15.3.0.0")}),1.0]])]});
            var Q7;
            Q7=makeQuery(id+"F5.imprint","IMPRINT",FACE,{"disambiguationData":[TD([[makeQuery(id+"F5.imprint","IMPRINT",EDGE,{"derivedFrom":sQuery(id+"F5.wireOp",EDGE,"E15.4.0.0")}),1.0]])]});
            var Q8;
            Q8=makeQuery(id+"F5.imprint","IMPRINT",FACE,{"disambiguationData":[TD([[makeQuery(id+"F5.imprint","IMPRINT",EDGE,{"derivedFrom":sQuery(id+"F5.wireOp",EDGE,"E15.5.0.0")}),1.0]])]});
            var Q9;
            Q9=makeQuery(id+"F5.imprint","IMPRINT",FACE,{"disambiguationData":[TD([[makeQuery(id+"F5.imprint","IMPRINT",EDGE,{"derivedFrom":sQuery(id+"F5.wireOp",EDGE,"E15.6.0.0")}),1.0]])]});
            var Q10;
            Q10=makeQuery(id+"F5.imprint","IMPRINT",FACE,{"disambiguationData":[TD([[makeQuery(id+"F5.imprint","IMPRINT",EDGE,{"derivedFrom":sQuery(id+"F5.wireOp",EDGE,"E15.7.0.0")}),1.0]])]});
            var Q11;
            Q11=makeQuery(id+"F5.imprint","IMPRINT",FACE,{"disambiguationData":[TD([[makeQuery(id+"F5.imprint","IMPRINT",EDGE,{"derivedFrom":sQuery(id+"F5.wireOp",EDGE,"E15.8.0.0")}),1.0]])]});
            var Q12;
            Q12=makeQuery(id+"F5.imprint","IMPRINT",FACE,{"disambiguationData":[TD([[makeQuery(id+"F5.imprint","IMPRINT",EDGE,{"derivedFrom":sQuery(id+"F5.wireOp",EDGE,"E15.9.0.0")}),1.0]])]});
            var Q13;
            Q13=makeQuery(id+"F5.imprint","IMPRINT",FACE,{"disambiguationData":[TD([[makeQuery(id+"F5.imprint","IMPRINT",EDGE,{"derivedFrom":sQuery(id+"F5.wireOp",EDGE,"E16.0.10.0")}),1.0]])]});
            var Q14;
            Q14=makeQuery(id+"F5.imprint","IMPRINT",FACE,{"disambiguationData":[TD([[makeQuery(id+"F5.imprint","IMPRINT",EDGE,{"derivedFrom":sQuery(id+"F5.wireOp",EDGE,"E17.0.11.0")}),1.0]])]});
            var Q15;
            Q15=makeQuery(id+"F5.imprint","IMPRINT",FACE,{"disambiguationData":[TD([[makeQuery(id+"F5.imprint","IMPRINT",EDGE,{"derivedFrom":sQuery(id+"F5.wireOp",EDGE,"E17.0.11.1")}),1.0]])]});
            var Q16;
            Q16=makeQuery(id+"F5.imprint","IMPRINT",FACE,{"disambiguationData":[TD([[makeQuery(id+"F5.imprint","IMPRINT",EDGE,{"derivedFrom":sQuery(id+"F5.wireOp",EDGE,"E16.0.10.1")}),1.0]])]});
            var Q17;
            Q17=makeQuery(id+"F5.imprint","IMPRINT",FACE,{"disambiguationData":[TD([[makeQuery(id+"F5.imprint","IMPRINT",EDGE,{"derivedFrom":sQuery(id+"F5.wireOp",EDGE,"E15.9.1.0")}),1.0]])]});
            var Q18;
            Q18=makeQuery(id+"F5.imprint","IMPRINT",FACE,{"disambiguationData":[TD([[makeQuery(id+"F5.imprint","IMPRINT",EDGE,{"derivedFrom":sQuery(id+"F5.wireOp",EDGE,"E15.8.1.0")}),1.0]])]});
            var Q19;
            Q19=makeQuery(id+"F5.imprint","IMPRINT",FACE,{"disambiguationData":[TD([[makeQuery(id+"F5.imprint","IMPRINT",EDGE,{"derivedFrom":sQuery(id+"F5.wireOp",EDGE,"E15.7.1.0")}),1.0]])]});
            var Q20;
            Q20=makeQuery(id+"F5.imprint","IMPRINT",FACE,{"disambiguationData":[TD([[makeQuery(id+"F5.imprint","IMPRINT",EDGE,{"derivedFrom":sQuery(id+"F5.wireOp",EDGE,"E15.6.1.0")}),1.0]])]});
            var Q21;
            Q21=makeQuery(id+"F5.imprint","IMPRINT",FACE,{"disambiguationData":[TD([[makeQuery(id+"F5.imprint","IMPRINT",EDGE,{"derivedFrom":sQuery(id+"F5.wireOp",EDGE,"E15.5.1.0")}),1.0]])]});
            var Q22;
            Q22=makeQuery(id+"F5.imprint","IMPRINT",FACE,{"disambiguationData":[TD([[makeQuery(id+"F5.imprint","IMPRINT",EDGE,{"derivedFrom":sQuery(id+"F5.wireOp",EDGE,"E15.4.1.0")}),1.0]])]});
            var Q23;
            Q23=makeQuery(id+"F5.imprint","IMPRINT",FACE,{"disambiguationData":[TD([[makeQuery(id+"F5.imprint","IMPRINT",EDGE,{"derivedFrom":sQuery(id+"F5.wireOp",EDGE,"E15.3.1.0")}),1.0]])]});
            extrude(context, id + "F6", {"entities" : qUnion([Q0, Q1, Q2, Q3, Q4, Q5, Q6, Q7, Q8, Q9, Q10, Q11, Q12, Q13, Q14, Q15, Q16, Q17, Q18, Q19, Q20, Q21, Q22, Q23]), "operationType" : NewBodyOperationType.REMOVE, "oppositeDirection" : true, "depth" : 25 * mm});
        }
    });
